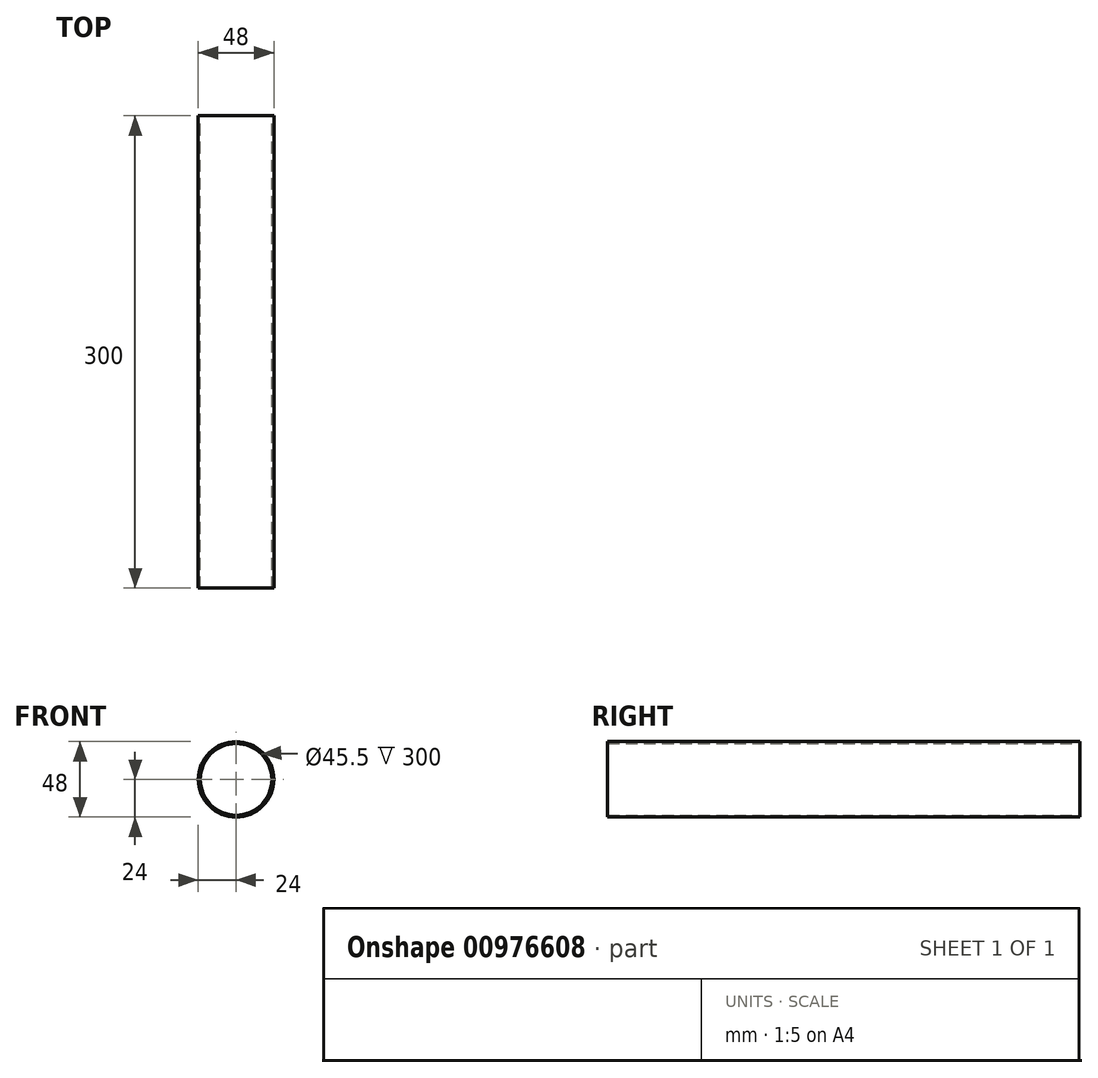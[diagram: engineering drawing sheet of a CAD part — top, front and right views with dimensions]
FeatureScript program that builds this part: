
annotation { "Feature Type Name" : "Feature", "Feature Type Description" : "" }
export const myFeature = defineFeature(function(context is Context, id is Id, definition is map)
    precondition{}
    {
        {
            var Q0;
            Q0=qCreatedBy(makeId("Front.planeOp"),FACE);
            var sketch = newSketch(context, id + "F0", { "sketchPlane" : qUnion([Q0])});
            skCircle(sketch, "E0", {"center": v(0, 0) * mm, "radius": 24 * mm});
            skCircle(sketch, "E1", {"center": v(0, 0) * mm, "radius": 22.75 * mm});
            skSolve(sketch);
        }
        {
            var Q0;
            Q0=makeQuery(id+"F0.imprint","IMPRINT",FACE,{"disambiguationData":[TD([[makeQuery(id+"F0.imprint","IMPRINT",EDGE,{"derivedFrom":sQuery(id+"F0.wireOp",EDGE,"E0")}),1.0]])]});
            extrude(context, id + "F1", {"entities" : qUnion([Q0]), "depth" : 300 * mm, "offsetDistance" : 25 * mm, "symmetric" : true});
        }
    });
